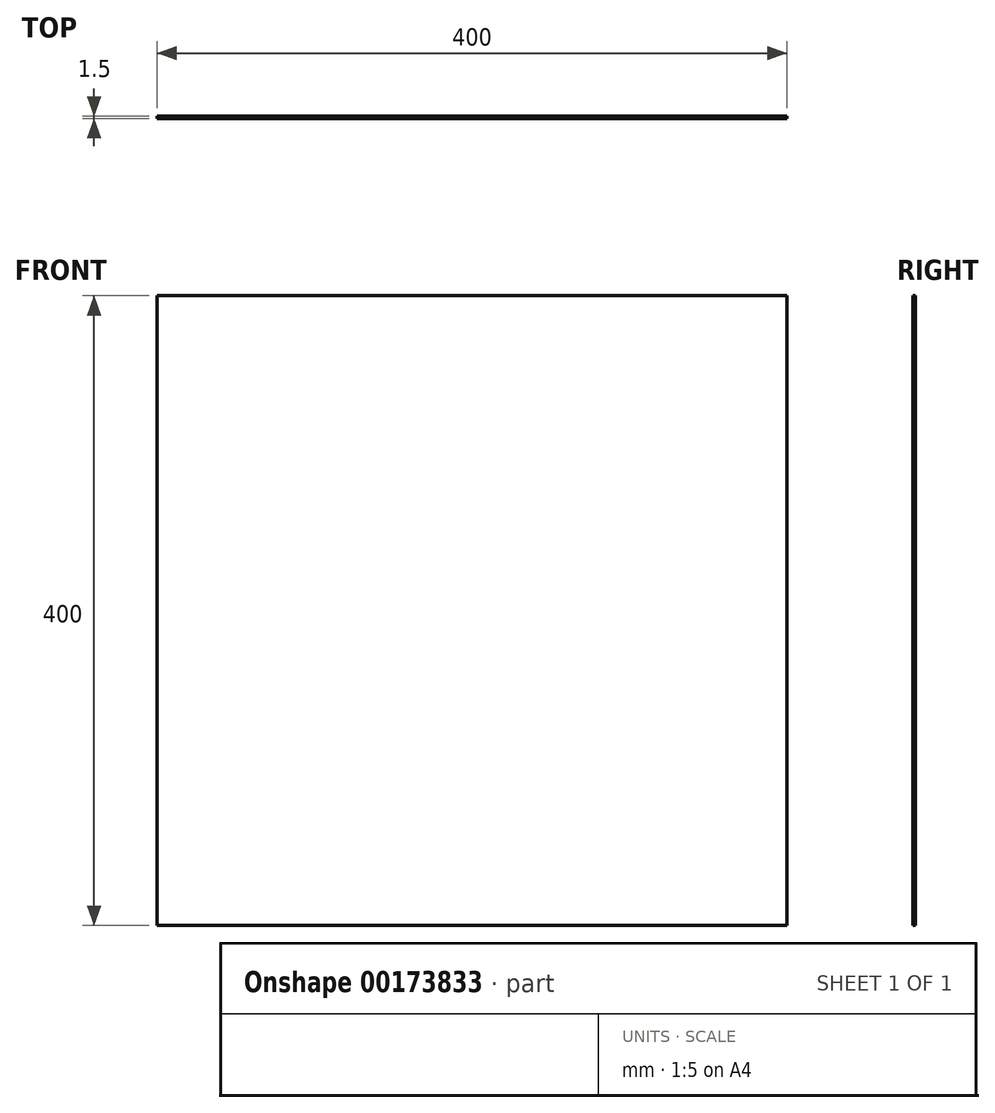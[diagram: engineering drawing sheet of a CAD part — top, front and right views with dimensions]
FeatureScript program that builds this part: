
annotation { "Feature Type Name" : "Feature", "Feature Type Description" : "" }
export const myFeature = defineFeature(function(context is Context, id is Id, definition is map)
    precondition{}
    {
        {
            var Q0;
            Q0=qCreatedBy(makeId("Front.planeOp"),FACE);
            var sketch = newSketch(context, id + "F0", { "sketchPlane" : qUnion([Q0])});
            skLineSegment(sketch, "E0.bottom", {"start": v(0, 0) * mm, "end": v(400, 0) * mm});
            skLineSegment(sketch, "E0.top", {"start": v(0, 400) * mm, "end": v(400, 400) * mm});
            skLineSegment(sketch, "E0.left", {"start": v(0, 0) * mm, "end": v(0, 400) * mm});
            skLineSegment(sketch, "E0.right", {"start": v(400, 0) * mm, "end": v(400, 400) * mm});
            skSolve(sketch);
        }
        {
            var Q0;
            Q0 = qSketchRegion(id + "F0", true);
            extrude(context, id + "F1", {"entities" : qUnion([Q0]), "depth" : 1.5 * mm});
        }
    });
